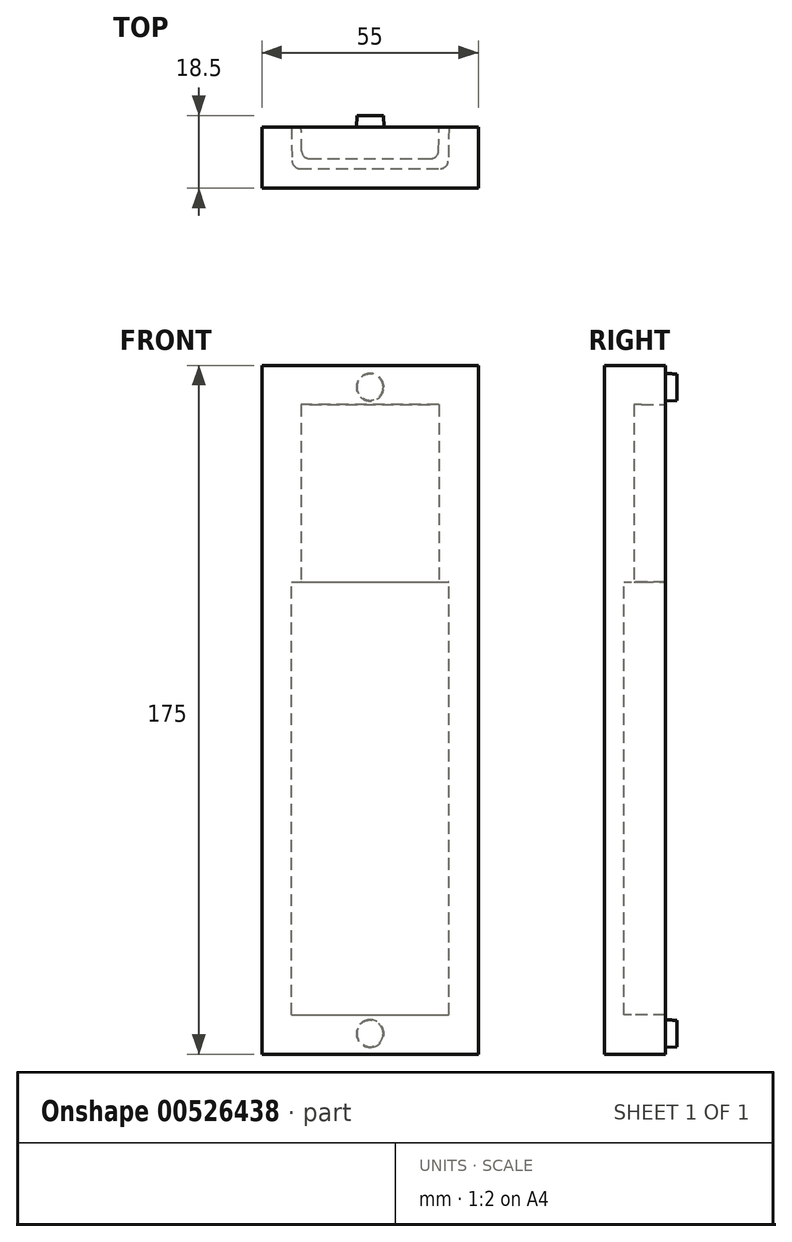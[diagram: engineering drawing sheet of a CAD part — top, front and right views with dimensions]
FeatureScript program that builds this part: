
annotation { "Feature Type Name" : "Feature", "Feature Type Description" : "" }
export const myFeature = defineFeature(function(context is Context, id is Id, definition is map)
    precondition{}
    {
        {
            var Q0;
            Q0=qCreatedBy(makeId("Top.planeOp"),FACE);
            var sketch = newSketch(context, id + "F0", { "sketchPlane" : qUnion([Q0])});
            skLineSegment(sketch, "E0.bottom", {"start": v(25, -13) * mm, "end": v(-25, -13) * mm});
            skLineSegment(sketch, "E0.top", {"start": v(25, 13) * mm, "end": v(-25, 13) * mm});
            skLineSegment(sketch, "E0.left", {"start": v(25, -13) * mm, "end": v(25, 13) * mm});
            skLineSegment(sketch, "E0.right", {"start": v(-25, -13) * mm, "end": v(-25, 13) * mm});
            skPoint(sketch, "E0.middle", {"position": v(0, 0) * mm});
            skSolve(sketch);
        }
        {
            var Q0;
            Q0 = qSketchRegion(id + "F0", true);
            extrude(context, id + "F1", {"entities" : qUnion([Q0]), "depth" : 55 * mm, "offsetDistance" : 25 * mm});
        }
        {
            var Q0;
            Q0=makeQuery(id+"F1.opExtrude","CAP_FACE",FACE,{"disambiguationData":[OSD([sQuery(id+"F0.wireOp",EDGE,"E0.bottom"),sQuery(id+"F0.wireOp",EDGE,"E0.top"),sQuery(id+"F0.wireOp",EDGE,"E0.left"),sQuery(id+"F0.wireOp",EDGE,"E0.right")])],"isStart":true});
            var sketch = newSketch(context, id + "F2", { "sketchPlane" : qUnion([Q0])});
            skPoint(sketch, "E1.middle", {"position": v(0, 0) * mm});
            skLineSegment(sketch, "E2", {"start": v(17.36, -8) * mm, "end": v(17.5, 0) * mm});
            skLineSegment(sketch, "E3", {"start": v(-17.36, -8) * mm, "end": v(-17.5, 0) * mm});
            skLineSegment(sketch, "E4", {"start": v(-17.36, 8) * mm, "end": v(-17.5, 0) * mm});
            skLineSegment(sketch, "E5", {"start": v(17.36, 8) * mm, "end": v(17.5, 0) * mm});
            skLineSegment(sketch, "E6", {"start": v(-17.36, 8) * mm, "end": v(17.36, 8) * mm});
            skLineSegment(sketch, "E7", {"start": v(-17.36, -8) * mm, "end": v(17.36, -8) * mm});
            skSolve(sketch);
        }
        {
            var Q0;
            Q0 = qSketchRegion(id + "F2", true);
            extrude(context, id + "F3", {"entities" : qUnion([Q0]), "operationType" : NewBodyOperationType.REMOVE, "oppositeDirection" : true, "depth" : 45 * mm, "offsetDistance" : 25 * mm});
        }
        {
            var Q0;
            Q0=makeQuery(id+"F3.boolean.opBoolean","COPY",EDGE,{"derivedFrom":makeQuery(id+"F3.opExtrude","SWEPT_EDGE",EDGE,{"disambiguationData":[OSD([sQuery(id+"F2.wireOp",EDGE,"E3"),sQuery(id+"F2.wireOp",EDGE,"E7")])]})});
            var Q1;
            Q1=makeQuery(id+"F3.boolean.opBoolean","COPY",EDGE,{"derivedFrom":makeQuery(id+"F3.opExtrude","SWEPT_EDGE",EDGE,{"disambiguationData":[OSD([sQuery(id+"F2.wireOp",EDGE,"E2"),sQuery(id+"F2.wireOp",EDGE,"E7")])]})});
            fillet(context, id + "F4", {"entities" : qUnion([Q0, Q1]), "radius" : 2 * mm, "tangentPropagation" : true, "allowEdgeOverflow" : false});
        }
        {
            var Q0;
            Q0=makeQuery(id+"F3.boolean.opBoolean","COPY",EDGE,{"derivedFrom":makeQuery(id+"F3.opExtrude","SWEPT_EDGE",EDGE,{"disambiguationData":[OSD([sQuery(id+"F2.wireOp",EDGE,"E4"),sQuery(id+"F2.wireOp",EDGE,"E6")])]})});
            var Q1;
            Q1=makeQuery(id+"F3.boolean.opBoolean","COPY",EDGE,{"derivedFrom":makeQuery(id+"F3.opExtrude","SWEPT_EDGE",EDGE,{"disambiguationData":[OSD([sQuery(id+"F2.wireOp",EDGE,"E5"),sQuery(id+"F2.wireOp",EDGE,"E6")])]})});
            fillet(context, id + "F5", {"entities" : qUnion([Q0, Q1]), "radius" : 2 * mm, "tangentPropagation" : true, "allowEdgeOverflow" : false});
        }
        {
            var Q0;
            Q0=makeQuery(id+"F1.opExtrude","CAP_FACE",FACE,{"disambiguationData":[OSD([sQuery(id+"F0.wireOp",EDGE,"E0.bottom"),sQuery(id+"F0.wireOp",EDGE,"E0.top"),sQuery(id+"F0.wireOp",EDGE,"E0.left"),sQuery(id+"F0.wireOp",EDGE,"E0.right")])],"isStart":true});
            var sketch = newSketch(context, id + "F6", { "sketchPlane" : qUnion([Q0])});
            skLineSegment(sketch, "E8.bottom", {"start": v(27.5, -15.5) * mm, "end": v(-27.5, -15.5) * mm});
            skLineSegment(sketch, "E8.top", {"start": v(27.5, 15.5) * mm, "end": v(-27.5, 15.5) * mm});
            skLineSegment(sketch, "E8.left", {"start": v(27.5, -15.5) * mm, "end": v(27.5, 15.5) * mm});
            skLineSegment(sketch, "E8.right", {"start": v(-27.5, -15.5) * mm, "end": v(-27.5, 15.5) * mm});
            skPoint(sketch, "E8.middle", {"position": v(0, 0) * mm});
            skSolve(sketch);
        }
        {
            var Q0;
            Q0 = qSketchRegion(id + "F6", true);
            extrude(context, id + "F7", {"entities" : qUnion([Q0]), "operationType" : NewBodyOperationType.ADD, "depth" : 120 * mm, "offsetDistance" : 25 * mm});
        }
        {
            var Q0;
            {var subQ0=sQuery(id+"F6.wireOp",EDGE,"E8.bottom");var subQ1=sQuery(id+"F6.wireOp",EDGE,"E8.top");var subQ2=sQuery(id+"F6.wireOp",EDGE,"E8.left");var subQ3=sQuery(id+"F6.wireOp",EDGE,"E8.right");Q0=makeQuery(id+"F7.boolean.opBoolean","SPLIT",FACE,{"disambiguationData":[TD([makeQuery(id+"F1.opExtrude","SWEPT_FACE",FACE,{"disambiguationData":[OSD([sQuery(id+"F0.wireOp",EDGE,"E0.bottom")])]})])],"derivedFrom":makeQuery(id+"F7.opExtrude","CAP_FACE",FACE,{"disambiguationData":[OSD([subQ0,subQ1,subQ2,subQ3])],"isStart":true})});}
            var sketch = newSketch(context, id + "F8", { "sketchPlane" : qUnion([Q0])});
            skPoint(sketch, "E9.middle", {"position": v(0, 0) * mm});
            skLineSegment(sketch, "E10", {"start": v(-20, 0) * mm, "end": v(-19.82, -10.5) * mm});
            skLineSegment(sketch, "E11", {"start": v(20, 0) * mm, "end": v(19.82, -10.5) * mm});
            skLineSegment(sketch, "E12", {"start": v(19.82, 10.5) * mm, "end": v(20, 0) * mm});
            skLineSegment(sketch, "E13", {"start": v(-20, 0) * mm, "end": v(-19.82, 10.5) * mm});
            skLineSegment(sketch, "E14", {"start": v(-19.82, -10.5) * mm, "end": v(19.82, -10.5) * mm});
            skLineSegment(sketch, "E15", {"start": v(-19.82, 10.5) * mm, "end": v(19.82, 10.5) * mm});
            skSolve(sketch);
        }
        {
            var Q0;
            Q0 = qSketchRegion(id + "F8", true);
            extrude(context, id + "F9", {"entities" : qUnion([Q0]), "operationType" : NewBodyOperationType.REMOVE, "oppositeDirection" : true, "depth" : 110 * mm, "offsetDistance" : 25 * mm});
        }
        {
            var Q0;
            Q0=makeQuery(id+"F9.boolean.opBoolean","COPY",EDGE,{"derivedFrom":makeQuery(id+"F9.opExtrude","SWEPT_EDGE",EDGE,{"disambiguationData":[OSD([sQuery(id+"F8.wireOp",EDGE,"E10"),sQuery(id+"F8.wireOp",EDGE,"E14")])]})});
            var Q1;
            Q1=makeQuery(id+"F9.boolean.opBoolean","COPY",EDGE,{"derivedFrom":makeQuery(id+"F9.opExtrude","SWEPT_EDGE",EDGE,{"disambiguationData":[OSD([sQuery(id+"F8.wireOp",EDGE,"E11"),sQuery(id+"F8.wireOp",EDGE,"E14")])]})});
            var Q2;
            Q2=makeQuery(id+"F9.boolean.opBoolean","COPY",EDGE,{"derivedFrom":makeQuery(id+"F9.opExtrude","SWEPT_EDGE",EDGE,{"disambiguationData":[OSD([sQuery(id+"F8.wireOp",EDGE,"E13"),sQuery(id+"F8.wireOp",EDGE,"E15")])]})});
            var Q3;
            Q3=makeQuery(id+"F9.boolean.opBoolean","COPY",EDGE,{"derivedFrom":makeQuery(id+"F9.opExtrude","SWEPT_EDGE",EDGE,{"disambiguationData":[OSD([sQuery(id+"F8.wireOp",EDGE,"E12"),sQuery(id+"F8.wireOp",EDGE,"E15")])]})});
            fillet(context, id + "F10", {"entities" : qUnion([Q0, Q1, Q2, Q3]), "radius" : 2 * mm, "tangentPropagation" : true, "allowEdgeOverflow" : false});
        }
        {
            var Q0;
            Q0=qCreatedBy(makeId("Front.planeOp"),FACE);
            var sketch = newSketch(context, id + "F11", { "sketchPlane" : qUnion([Q0])});
            skLineSegment(sketch, "E16.bottom", {"start": v(-94.89, 86.67) * mm, "end": v(98.98, 86.67) * mm});
            skLineSegment(sketch, "E16.top", {"start": v(-94.89, -148.46) * mm, "end": v(98.98, -148.46) * mm});
            skLineSegment(sketch, "E16.left", {"start": v(-94.89, 86.67) * mm, "end": v(-94.89, -148.46) * mm});
            skLineSegment(sketch, "E16.right", {"start": v(98.98, 86.67) * mm, "end": v(98.98, -148.46) * mm});
            skSolve(sketch);
        }
        {
            var Q0;
            Q0 = qSketchRegion(id + "F11", true);
            extrude(context, id + "F12", {"entities" : qUnion([Q0]), "operationType" : NewBodyOperationType.REMOVE, "endBound" : BoundingType.THROUGH_ALL, "oppositeDirection" : true, "depth" : 25 * mm, "offsetDistance" : 25 * mm});
        }
        {
            var Q0;
            Q0=makeQuery(id+"F12.boolean.opBoolean","COPY",FACE,{"derivedFrom":makeQuery(id+"F12.opExtrude","CAP_FACE",FACE,{"disambiguationData":[OSD([sQuery(id+"F11.wireOp",EDGE,"E16.bottom"),sQuery(id+"F11.wireOp",EDGE,"E16.top"),sQuery(id+"F11.wireOp",EDGE,"E16.left"),sQuery(id+"F11.wireOp",EDGE,"E16.right")])],"isStart":true})});
            var sketch = newSketch(context, id + "F13", { "sketchPlane" : qUnion([Q0])});
            skCircle(sketch, "E17", {"center": v(0, 49.44) * mm, "radius": 3.5 * mm});
            skSolve(sketch);
        }
        {
            var Q0;
            Q0 = qSketchRegion(id + "F13", true);
            extrude(context, id + "F14", {"entities" : qUnion([Q0]), "operationType" : NewBodyOperationType.ADD, "depth" : 3 * mm, "offsetDistance" : 25 * mm, "hasDraft" : true, "draftAngle" : 3 * degree, "draftPullDirection" : true});
        }
        {
            var Q0;
            Q0=makeQuery(id+"F12.boolean.opBoolean","COPY",FACE,{"derivedFrom":makeQuery(id+"F12.opExtrude","CAP_FACE",FACE,{"disambiguationData":[OSD([sQuery(id+"F11.wireOp",EDGE,"E16.bottom"),sQuery(id+"F11.wireOp",EDGE,"E16.top"),sQuery(id+"F11.wireOp",EDGE,"E16.left"),sQuery(id+"F11.wireOp",EDGE,"E16.right")])],"isStart":true})});
            var sketch = newSketch(context, id + "F15", { "sketchPlane" : qUnion([Q0])});
            skCircle(sketch, "E18", {"center": v(0, -114.77) * mm, "radius": 3.5 * mm});
            skSolve(sketch);
        }
        {
            var Q0;
            Q0 = qSketchRegion(id + "F15", true);
            extrude(context, id + "F16", {"entities" : qUnion([Q0]), "operationType" : NewBodyOperationType.ADD, "depth" : 3 * mm, "offsetDistance" : 25 * mm, "hasDraft" : true, "draftAngle" : 3 * degree, "draftPullDirection" : true});
        }
        {
            var Q0;
            {var subQ0=sQuery(id+"F6.wireOp",EDGE,"E8.bottom");var subQ1=sQuery(id+"F6.wireOp",EDGE,"E8.top");var subQ2=sQuery(id+"F6.wireOp",EDGE,"E8.left");var subQ3=sQuery(id+"F6.wireOp",EDGE,"E8.right");Q0=makeQuery(id+"F7.boolean.opBoolean","SPLIT",FACE,{"disambiguationData":[TD([makeQuery(id+"F1.opExtrude","SWEPT_FACE",FACE,{"disambiguationData":[OSD([sQuery(id+"F0.wireOp",EDGE,"E0.bottom")])]})])],"derivedFrom":makeQuery(id+"F7.opExtrude","CAP_FACE",FACE,{"disambiguationData":[OSD([subQ0,subQ1,subQ2,subQ3])],"isStart":true})});}
            var sketch = newSketch(context, id + "F17", { "sketchPlane" : qUnion([Q0])});
            skSolve(sketch);
        }
        {
            var Q0;
            Q0 = qSketchRegion(id + "F17", true);
            var Q1;
            {var subQ3=sQuery(id+"F6.wireOp",EDGE,"E8.top");Q1=makeQuery(id+"F17.imprint","IMPRINT",FACE,{"disambiguationData":[TD([[makeQuery(id+"F17.imprint","IMPRINT",EDGE,{"derivedFrom":makeQuery(id+"F7.opExtrude","CAP_EDGE",EDGE,{"disambiguationData":[OSD([subQ3])],"isStart":true})}),-1.0]])]});}
            var Q2;
            Q2=makeQuery(id+"F1.opExtrude","CAP_FACE",FACE,{"disambiguationData":[OSD([sQuery(id+"F0.wireOp",EDGE,"E0.bottom"),sQuery(id+"F0.wireOp",EDGE,"E0.top"),sQuery(id+"F0.wireOp",EDGE,"E0.left"),sQuery(id+"F0.wireOp",EDGE,"E0.right")])],"isStart":false});
            extrude(context, id + "F18", {"entities" : qUnion([Q0, Q1]), "operationType" : NewBodyOperationType.ADD, "endBound" : BoundingType.UP_TO_SURFACE, "depth" : 25 * mm, "endBoundEntityFace" : qUnion([Q2]), "offsetDistance" : 25 * mm});
        }
    });
